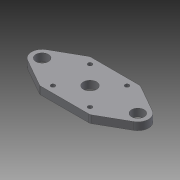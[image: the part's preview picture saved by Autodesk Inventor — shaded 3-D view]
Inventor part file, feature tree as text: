
AUTODESK INVENTOR PART (.ipt)
format: ipt  version: 2015 (Build 190159000, 159)  size: 123,904 bytes
history: native  units: in
note: dims shown in document units (in); Inventor stores cm internally (conversion verified against a paired STEP export)
features: extrude x2, sketch x2, fillet x1
ambient origin geometry x8: Origin, YZ Plane, XZ Plane, XY Plane, X Axis, Y Axis, Z Axis, Center Point
bodies: Body1 (feature_tree)
feature tree (5):
  extrude  "Extrusion4"  Depth=1.6535in
  extrude  "Extrusion5"  Depth=0.125in
  fillet  "Fillet1"  Radius=0.25in
  sketch  "Sketch1"  dims[d0=1.6535in d1=1.6535in]
  sketch  "Sketch2"  dims[d4=0.1378in d8=0.4331in d11=0.25in d12=0.0in d13=1.2205in d16=1.0in d17=0.0in d18=0.4134in d20=3.1496in d21=0.35in d22=0.125in]
